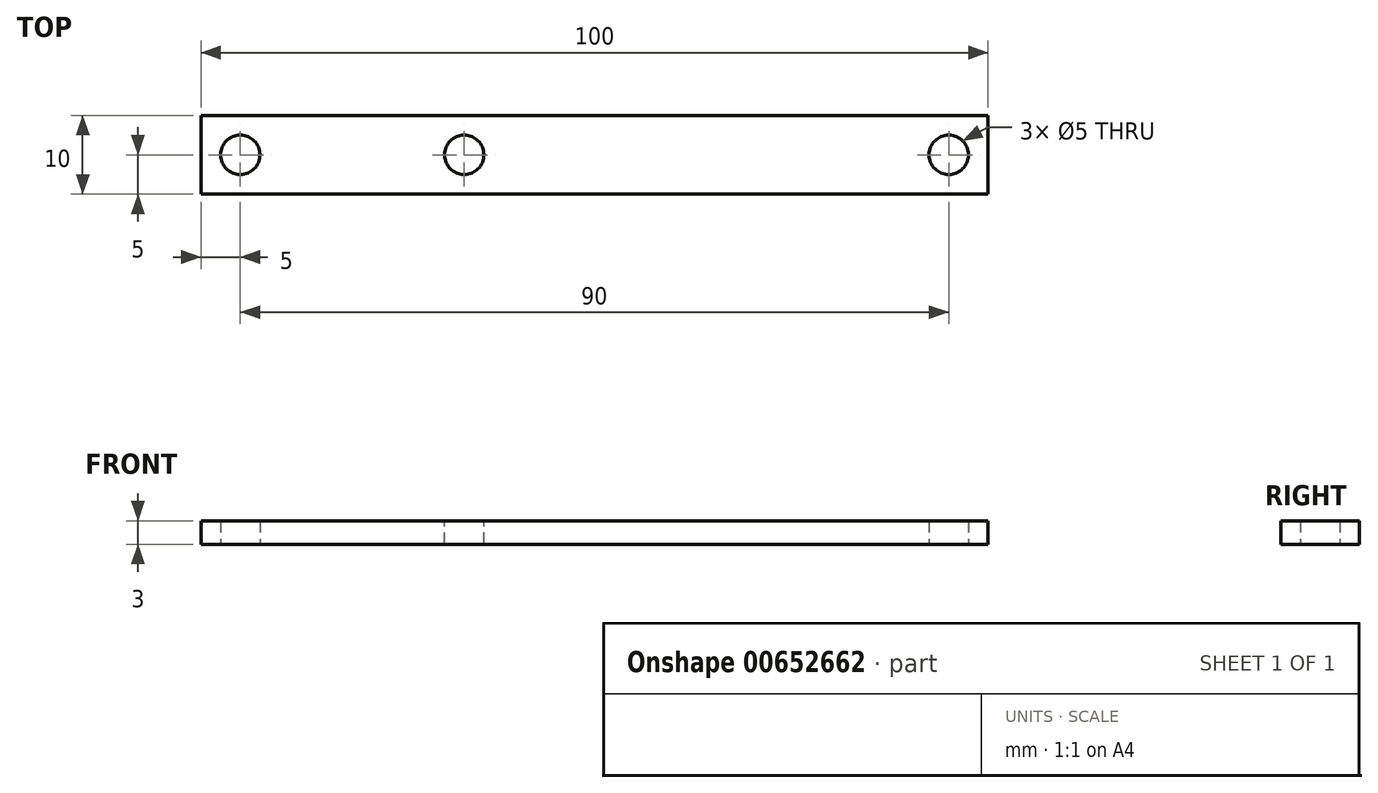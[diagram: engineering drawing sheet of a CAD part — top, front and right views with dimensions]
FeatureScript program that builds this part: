
annotation { "Feature Type Name" : "Feature", "Feature Type Description" : "" }
export const myFeature = defineFeature(function(context is Context, id is Id, definition is map)
    precondition{}
    {
        {
            var Q0;
            Q0=qCreatedBy(makeId("Top.planeOp"),FACE);
            var sketch = newSketch(context, id + "F0", { "sketchPlane" : qUnion([Q0])});
            skLineSegment(sketch, "E0.bottom", {"start": v(50, -5) * mm, "end": v(-50, -5) * mm});
            skLineSegment(sketch, "E0.top", {"start": v(50, 5) * mm, "end": v(-50, 5) * mm});
            skLineSegment(sketch, "E0.left", {"start": v(50, -5) * mm, "end": v(50, 5) * mm});
            skLineSegment(sketch, "E0.right", {"start": v(-50, -5) * mm, "end": v(-50, 5) * mm});
            skPoint(sketch, "E0.middle", {"position": v(0, 0) * mm});
            skCircle(sketch, "E1", {"center": v(-45, 0) * mm, "radius": 2.5 * mm});
            skPoint(sketch, "E1.centerSnap0", {"position": v(-50, 0) * mm});
            skCircle(sketch, "E2", {"center": v(45, 0) * mm, "radius": 2.5 * mm});
            skLineSegment(sketch, "E3", {"start": v(-50, 0) * mm, "end": v(-45, 0) * mm, "construction": true});
            skLineSegment(sketch, "E4", {"start": v(-45, 5) * mm, "end": v(-45, 0) * mm, "construction": true});
            skLineSegment(sketch, "E5", {"start": v(45, 5) * mm, "end": v(45, 0) * mm, "construction": true});
            skLineSegment(sketch, "E6", {"start": v(50, 0) * mm, "end": v(45, 0) * mm, "construction": true});
            skSolve(sketch);
        }
        {
            var Q0;
            Q0=makeQuery(id+"F0.imprint","IMPRINT",FACE,{"disambiguationData":[TD([[makeQuery(id+"F0.imprint","IMPRINT",EDGE,{"derivedFrom":sQuery(id+"F0.wireOp",EDGE,"E0.bottom")}),-1.0]])]});
            extrude(context, id + "F1", {"entities" : qUnion([Q0]), "depth" : 3 * mm, "offsetDistance" : 25 * mm});
        }
        {
            var Q0;
            Q0=makeQuery(id+"F1.opExtrude","CAP_FACE",FACE,{"disambiguationData":[OSD([sQuery(id+"F0.wireOp",EDGE,"E0.bottom"),sQuery(id+"F0.wireOp",EDGE,"E0.top"),sQuery(id+"F0.wireOp",EDGE,"E0.left"),sQuery(id+"F0.wireOp",EDGE,"E0.right"),sQuery(id+"F0.wireOp",EDGE,"E1"),sQuery(id+"F0.wireOp",EDGE,"E2")])],"isStart":false});
            var sketch = newSketch(context, id + "F2", { "sketchPlane" : qUnion([Q0])});
            skCircle(sketch, "E7", {"center": v(-16.55, 0) * mm, "radius": 2.5 * mm});
            skLineSegment(sketch, "E8", {"start": v(-45, 0) * mm, "end": v(-16.55, 0) * mm, "construction": true});
            skSolve(sketch);
        }
        {
            var Q0;
            Q0=makeQuery(id+"F2.imprint","IMPRINT",FACE,{"disambiguationData":[TD([[makeQuery(id+"F2.imprint","IMPRINT",EDGE,{"derivedFrom":sQuery(id+"F2.wireOp",EDGE,"E7")}),1.0]])]});
            extrude(context, id + "F3", {"entities" : qUnion([Q0]), "operationType" : NewBodyOperationType.REMOVE, "oppositeDirection" : true, "depth" : 3 * mm, "offsetDistance" : 25 * mm});
        }
    });
